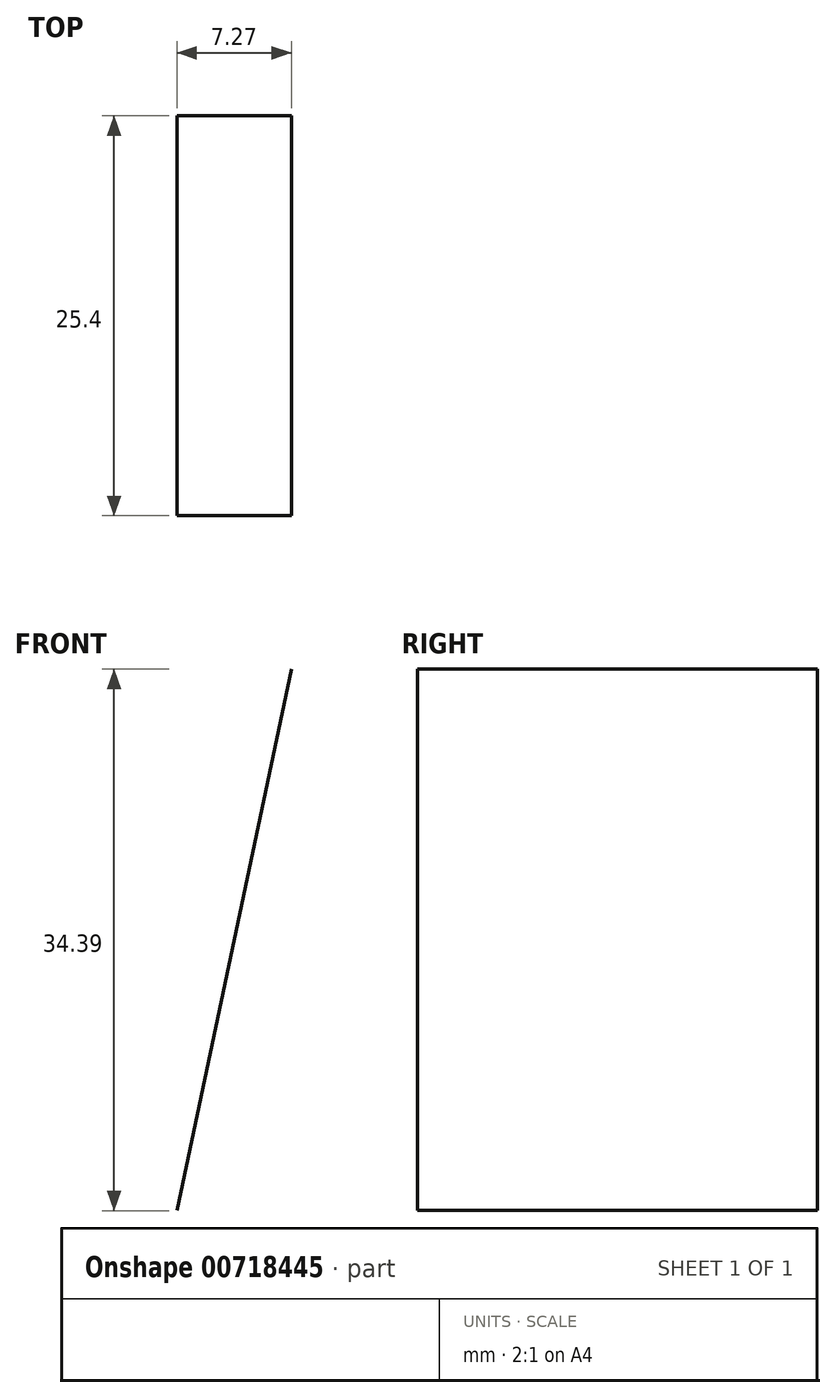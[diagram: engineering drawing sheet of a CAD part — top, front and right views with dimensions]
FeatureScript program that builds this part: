
annotation { "Feature Type Name" : "Feature", "Feature Type Description" : "" }
export const myFeature = defineFeature(function(context is Context, id is Id, definition is map)
    precondition{}
    {
        {
            var Q0;
            Q0=qCreatedBy(makeId("Front.planeOp"),FACE);
            var sketch = newSketch(context, id + "F0", { "sketchPlane" : qUnion([Q0])});
            skLineSegment(sketch, "E0", {"start": v(0, 0) * mm, "end": v(0, 101.1) * mm, "construction": true});
            skLineSegment(sketch, "E1", {"start": v(0, 0) * mm, "end": v(70.8, 0) * mm, "construction": true});
            skCircle(sketch, "E2", {"center": v(70.8, 0) * mm, "radius": 7.94 * mm});
            skCircle(sketch, "E3", {"center": v(0, 0) * mm, "radius": 9.53 * mm});
            skCircle(sketch, "E4", {"center": v(0, 101.1) * mm, "radius": 9.53 * mm});
            skCircle(sketch, "E5", {"center": v(0, 69.26) * mm, "radius": 15.88 * mm});
            skLineSegment(sketch, "E6", {"start": v(-9.52, 100.96) * mm, "end": v(-16.8, 66.57) * mm});
            skLineSegment(sketch, "E7", {"start": v(9.18, 103.63) * mm, "end": v(15.55, 72.43) * mm});
            skLineSegment(sketch, "E8", {"start": v(15.55, 72.43) * mm, "end": v(9.56, 0) * mm});
            skLineSegment(sketch, "E9", {"start": v(-16.8, 66.57) * mm, "end": v(-9.58, 0) * mm});
            skLineSegment(sketch, "E10", {"start": v(0, -9.53) * mm, "end": v(70.97, -7.94) * mm});
            skLineSegment(sketch, "E11", {"start": v(0, 9.52) * mm, "end": v(70.97, 7.94) * mm});
            skCircle(sketch, "E12", {"center": v(0, 101.1) * mm, "radius": 3.18 * mm});
            skCircle(sketch, "E13", {"center": v(0, 69.26) * mm, "radius": 3.18 * mm});
            skCircle(sketch, "E14", {"center": v(0, 0) * mm, "radius": 3.18 * mm});
            skCircle(sketch, "E15", {"center": v(70.8, 0) * mm, "radius": 3.18 * mm});
            skSolve(sketch);
        }
        {
            var Q0;
            Q0=sQuery(id+"F0.wireOp",EDGE,"E6");
            extrude(context, id + "F1", {"bodyType" : ToolBodyType.SURFACE, "surfaceEntities" : qUnion([Q0]), "depth" : 25.4 * mm, "offsetDistance" : 25.4 * mm});
        }
    });
